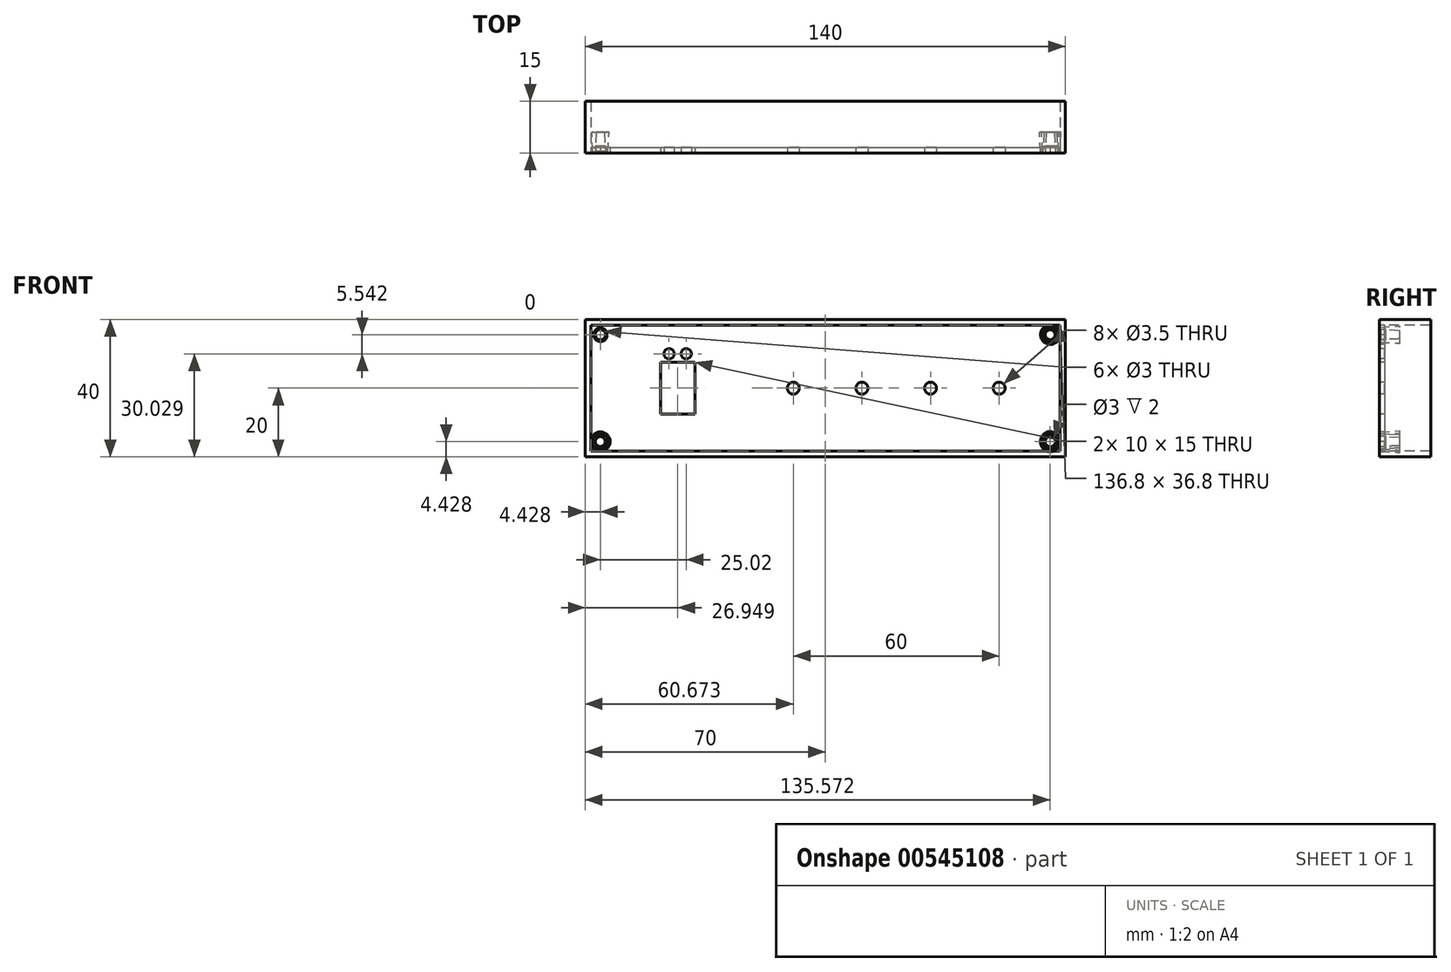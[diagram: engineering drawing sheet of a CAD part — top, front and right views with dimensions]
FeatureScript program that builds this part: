
annotation { "Feature Type Name" : "Feature", "Feature Type Description" : "" }
export const myFeature = defineFeature(function(context is Context, id is Id, definition is map)
    precondition{}
    {
        {
            var Q0;
            Q0=qCreatedBy(makeId("Front.planeOp"),FACE);
            var sketch = newSketch(context, id + "F0", { "sketchPlane" : qUnion([Q0])});
            skLineSegment(sketch, "E0.bottom", {"start": v(-70, 20) * mm, "end": v(70, 20) * mm});
            skLineSegment(sketch, "E0.top", {"start": v(-70, -20) * mm, "end": v(70, -20) * mm});
            skLineSegment(sketch, "E0.left", {"start": v(-70, 20) * mm, "end": v(-70, -20) * mm});
            skLineSegment(sketch, "E0.right", {"start": v(70, 20) * mm, "end": v(70, -20) * mm});
            skPoint(sketch, "E0.middle", {"position": v(0, 0) * mm});
            skLineSegment(sketch, "E1.bottom", {"start": v(-48.05, 7.5) * mm, "end": v(-38.05, 7.5) * mm});
            skLineSegment(sketch, "E1.top", {"start": v(-48.05, -7.5) * mm, "end": v(-38.05, -7.5) * mm});
            skLineSegment(sketch, "E1.left", {"start": v(-48.05, 7.5) * mm, "end": v(-48.05, -7.5) * mm});
            skLineSegment(sketch, "E1.right", {"start": v(-38.05, 7.5) * mm, "end": v(-38.05, -7.5) * mm});
            skPoint(sketch, "E1.middle", {"position": v(-43.05, 0) * mm});
            skCircle(sketch, "E2", {"center": v(-45.55, 10.03) * mm, "radius": 1.5 * mm});
            skCircle(sketch, "E3", {"center": v(-40.55, 10.03) * mm, "radius": 1.5 * mm});
            skPoint(sketch, "E4", {"position": v(-38.05, 0) * mm});
            skCircle(sketch, "E5", {"center": v(-9.33, 0) * mm, "radius": 1.75 * mm});
            skCircle(sketch, "E6", {"center": v(10.67, 0) * mm, "radius": 1.75 * mm});
            skCircle(sketch, "E7", {"center": v(30.67, 0) * mm, "radius": 1.75 * mm});
            skCircle(sketch, "E8", {"center": v(50.67, 0) * mm, "radius": 1.75 * mm});
            skLineSegment(sketch, "E9.0", {"start": v(-68.4, 18.4) * mm, "end": v(68.4, 18.4) * mm});
            skLineSegment(sketch, "E9.1", {"start": v(-68.4, 18.4) * mm, "end": v(-68.4, -18.4) * mm});
            skLineSegment(sketch, "E9.2", {"start": v(-68.4, -18.4) * mm, "end": v(68.4, -18.4) * mm});
            skLineSegment(sketch, "E9.3", {"start": v(68.4, 18.4) * mm, "end": v(68.4, -18.4) * mm});
            skCircle(sketch, "E10.MirrorC", {"center": v(65.57, 15.57) * mm, "radius": 2.83 * mm});
            skCircle(sketch, "E11.MirrorC", {"center": v(65.57, 15.57) * mm, "radius": 1.5 * mm});
            skCircle(sketch, "E12.MirrorC", {"center": v(-65.57, -15.57) * mm, "radius": 1.5 * mm});
            skCircle(sketch, "E13.MirrorC", {"center": v(-65.57, -15.57) * mm, "radius": 2.83 * mm});
            skCircle(sketch, "E14.MirrorC", {"center": v(65.57, -15.57) * mm, "radius": 1.5 * mm});
            skCircle(sketch, "E15.MirrorC", {"center": v(65.57, -15.57) * mm, "radius": 2.83 * mm});
            skCircle(sketch, "E16.MirrorC", {"center": v(65.57, 15.57) * mm, "radius": 2.18 * mm});
            skCircle(sketch, "E17.MirrorC", {"center": v(-65.57, -15.57) * mm, "radius": 2.18 * mm});
            skCircle(sketch, "E18.MirrorC", {"center": v(65.57, -15.57) * mm, "radius": 2.18 * mm});
            skPoint(sketch, "E19", {"position": v(-65.57, 15.57) * mm});
            skSolve(sketch);
        }
        {
            var Q0;
            Q0=makeQuery(id+"F0.imprint","IMPRINT",FACE,{"disambiguationData":[TD([[makeQuery(id+"F0.imprint","IMPRINT",EDGE,{"derivedFrom":sQuery(id+"F0.wireOp",EDGE,"E1.bottom")}),1.0]])]});
            var Q1;
            {var subQ0=sQuery(id+"F0.wireOp",EDGE,"nopY4PQG-6DAR-m26V-C0Me-koIEQxgehs8v");var subQ3=sQuery(id+"F0.wireOp",EDGE,"W0Mv9RJY-RmOc-FBdf-RBb3-klKlk9MDp93k");var subQ5=makeQuery(id+"F0.imprint","INTERSECT",VERTEX,{"derivedFrom":[subQ0,subQ3]});Q1=makeQuery(id+"F0.imprint","IMPRINT",FACE,{"disambiguationData":[TD([[makeQuery(id+"F0.imprint","IMPRINT",EDGE,{"disambiguationData":[TD([[subQ5,1.0]])],"derivedFrom":subQ3}),-1.0]])]});}
            var Q2;
            {var subQ0=sQuery(id+"F0.wireOp",EDGE,"nopY4PQG-6DAR-m26V-C0Me-koIEQxgehs8v");var subQ3=sQuery(id+"F0.wireOp",EDGE,"W0Mv9RJY-RmOc-FBdf-RBb3-klKlk9MDp93k");var subQ5=makeQuery(id+"F0.imprint","INTERSECT",VERTEX,{"derivedFrom":[subQ0,subQ3]});Q2=makeQuery(id+"F0.imprint","IMPRINT",FACE,{"disambiguationData":[TD([[makeQuery(id+"F0.imprint","IMPRINT",EDGE,{"disambiguationData":[TD([[subQ5,-1.0]])],"derivedFrom":subQ3}),-1.0]])]});}
            var Q3;
            {var subQ0=sQuery(id+"F0.wireOp",EDGE,"ZPrOADm0-ys7W-Uhxx-ERF7-CDe04Jh97fXN");var subQ3=sQuery(id+"F0.wireOp",EDGE,"JCLg79E9-NYku-jiiS-Y2hP-Kjt8igKviUym");var subQ5=makeQuery(id+"F0.imprint","INTERSECT",VERTEX,{"derivedFrom":[subQ0,subQ3]});Q3=makeQuery(id+"F0.imprint","IMPRINT",FACE,{"disambiguationData":[TD([[makeQuery(id+"F0.imprint","IMPRINT",EDGE,{"disambiguationData":[TD([[subQ5,1.0]])],"derivedFrom":subQ3}),-1.0]])]});}
            var Q4;
            {var subQ0=sQuery(id+"F0.wireOp",EDGE,"ZPrOADm0-ys7W-Uhxx-ERF7-CDe04Jh97fXN");var subQ3=sQuery(id+"F0.wireOp",EDGE,"JCLg79E9-NYku-jiiS-Y2hP-Kjt8igKviUym");var subQ5=makeQuery(id+"F0.imprint","INTERSECT",VERTEX,{"derivedFrom":[subQ0,subQ3]});Q4=makeQuery(id+"F0.imprint","IMPRINT",FACE,{"disambiguationData":[TD([[makeQuery(id+"F0.imprint","IMPRINT",EDGE,{"disambiguationData":[TD([[subQ5,-1.0]])],"derivedFrom":subQ3}),-1.0]])]});}
            var Q5;
            {var subQ0=sQuery(id+"F0.wireOp",EDGE,"IZJqcF3K-3XQc-JsiF-ESKG-TtM9fcgNwguu");var subQ3=sQuery(id+"F0.wireOp",EDGE,"lmyyJW9V-CXFS-4CVU-ZTqX-mRt5hHccTXIb");var subQ5=makeQuery(id+"F0.imprint","INTERSECT",VERTEX,{"derivedFrom":[subQ0,subQ3]});Q5=makeQuery(id+"F0.imprint","IMPRINT",FACE,{"disambiguationData":[TD([[makeQuery(id+"F0.imprint","IMPRINT",EDGE,{"disambiguationData":[TD([[subQ5,1.0]])],"derivedFrom":subQ3}),-1.0]])]});}
            var Q6;
            {var subQ0=sQuery(id+"F0.wireOp",EDGE,"IZJqcF3K-3XQc-JsiF-ESKG-TtM9fcgNwguu");var subQ3=sQuery(id+"F0.wireOp",EDGE,"lmyyJW9V-CXFS-4CVU-ZTqX-mRt5hHccTXIb");var subQ5=makeQuery(id+"F0.imprint","INTERSECT",VERTEX,{"derivedFrom":[subQ0,subQ3]});Q6=makeQuery(id+"F0.imprint","IMPRINT",FACE,{"disambiguationData":[TD([[makeQuery(id+"F0.imprint","IMPRINT",EDGE,{"disambiguationData":[TD([[subQ5,-1.0]])],"derivedFrom":subQ3}),-1.0]])]});}
            var Q7;
            {var subQ0=sQuery(id+"F0.wireOp",EDGE,"YOfMEWm0-9Egn-xnX8-rI6g-tOub0sCru1eY");var subQ3=sQuery(id+"F0.wireOp",EDGE,"njUcSJY2-imL9-KRpb-pFf1-RJkt4fxxxRg6");var subQ5=makeQuery(id+"F0.imprint","INTERSECT",VERTEX,{"derivedFrom":[subQ0,subQ3]});Q7=makeQuery(id+"F0.imprint","IMPRINT",FACE,{"disambiguationData":[TD([[makeQuery(id+"F0.imprint","IMPRINT",EDGE,{"disambiguationData":[TD([[subQ5,1.0]])],"derivedFrom":subQ3}),-1.0]])]});}
            var Q8;
            {var subQ0=sQuery(id+"F0.wireOp",EDGE,"YOfMEWm0-9Egn-xnX8-rI6g-tOub0sCru1eY");var subQ3=sQuery(id+"F0.wireOp",EDGE,"njUcSJY2-imL9-KRpb-pFf1-RJkt4fxxxRg6");var subQ5=makeQuery(id+"F0.imprint","INTERSECT",VERTEX,{"derivedFrom":[subQ0,subQ3]});Q8=makeQuery(id+"F0.imprint","IMPRINT",FACE,{"disambiguationData":[TD([[makeQuery(id+"F0.imprint","IMPRINT",EDGE,{"disambiguationData":[TD([[subQ5,-1.0]])],"derivedFrom":subQ3}),-1.0]])]});}
            extrude(context, id + "F1", {"entities" : qUnion([Q0, Q1, Q2, Q3, Q4, Q5, Q6, Q7, Q8]), "oppositeDirection" : true, "depth" : 1.6 * mm, "offsetDistance" : 25 * mm});
        }
        {
            var Q0;
            Q0=makeQuery(id+"F0.imprint","IMPRINT",FACE,{"disambiguationData":[TD([[makeQuery(id+"F0.imprint","IMPRINT",EDGE,{"derivedFrom":sQuery(id+"F0.wireOp",EDGE,"E0.bottom")}),-1.0]])]});
            extrude(context, id + "F2", {"entities" : qUnion([Q0]), "oppositeDirection" : true, "depth" : 15 * mm, "offsetDistance" : 25 * mm});
        }
        {
            var Q0;
            Q0=makeQuery(id+"F0.imprint","IMPRINT",FACE,{"disambiguationData":[TD([[makeQuery(id+"F0.imprint","IMPRINT",EDGE,{"derivedFrom":sQuery(id+"F0.wireOp",EDGE,"E1.bottom")}),1.0]])]});
            var Q1;
            {var subQ0=sQuery(id+"F0.wireOp",EDGE,"E9.1");var subQ1=sQuery(id+"F0.wireOp",EDGE,"E9.0");var subQ2=makeQuery(id+"F0.imprint","INTERSECT",VERTEX,{"derivedFrom":[subQ1,subQ0]});Q1=makeQuery(id+"F0.imprint","IMPRINT",FACE,{"disambiguationData":[TD([[makeQuery(id+"F0.imprint","IMPRINT",EDGE,{"disambiguationData":[TD([[subQ2,-1.0]])],"derivedFrom":subQ1}),-1.0]])]});}
            var Q2;
            {var subQ0=sQuery(id+"F0.wireOp",EDGE,"E9.2");var subQ1=sQuery(id+"F0.wireOp",EDGE,"E9.1");var subQ2=makeQuery(id+"F0.imprint","INTERSECT",VERTEX,{"derivedFrom":[subQ1,subQ0]});Q2=makeQuery(id+"F0.imprint","IMPRINT",FACE,{"disambiguationData":[TD([[makeQuery(id+"F0.imprint","IMPRINT",EDGE,{"disambiguationData":[TD([[subQ2,1.0]])],"derivedFrom":subQ1}),1.0]])]});}
            var Q3;
            {var subQ0=sQuery(id+"F0.wireOp",EDGE,"E9.3");var subQ1=sQuery(id+"F0.wireOp",EDGE,"E9.2");var subQ2=makeQuery(id+"F0.imprint","INTERSECT",VERTEX,{"derivedFrom":[subQ1,subQ0]});Q3=makeQuery(id+"F0.imprint","IMPRINT",FACE,{"disambiguationData":[TD([[makeQuery(id+"F0.imprint","IMPRINT",EDGE,{"disambiguationData":[TD([[subQ2,1.0]])],"derivedFrom":subQ1}),1.0]])]});}
            var Q4;
            {var subQ0=sQuery(id+"F0.wireOp",EDGE,"E9.3");var subQ1=sQuery(id+"F0.wireOp",EDGE,"E9.0");var subQ2=makeQuery(id+"F0.imprint","INTERSECT",VERTEX,{"derivedFrom":[subQ1,subQ0]});Q4=makeQuery(id+"F0.imprint","IMPRINT",FACE,{"disambiguationData":[TD([[makeQuery(id+"F0.imprint","IMPRINT",EDGE,{"disambiguationData":[TD([[subQ2,1.0]])],"derivedFrom":subQ1}),-1.0]])]});}
            extrude(context, id + "F3", {"entities" : qUnion([Q0, Q1, Q2, Q3, Q4]), "oppositeDirection" : true, "depth" : 1.6 * mm, "offsetDistance" : 25 * mm});
        }
        {
            var Q0;
            Q0=makeQuery(id+"F0.imprint","IMPRINT",FACE,{"disambiguationData":[TD([[makeQuery(id+"F0.imprint","IMPRINT",EDGE,{"derivedFrom":sQuery(id+"F0.wireOp",EDGE,"E16.MirrorC")}),1.0]])]});
            var Q1;
            Q1=makeQuery(id+"F0.imprint","IMPRINT",FACE,{"disambiguationData":[TD([[makeQuery(id+"F0.imprint","IMPRINT",EDGE,{"derivedFrom":sQuery(id+"F0.wireOp",EDGE,"E18.MirrorC")}),-1.0]])]});
            var Q2;
            Q2=makeQuery(id+"F0.imprint","IMPRINT",FACE,{"disambiguationData":[TD([[makeQuery(id+"F0.imprint","IMPRINT",EDGE,{"derivedFrom":sQuery(id+"F0.wireOp",EDGE,"E17.MirrorC")}),1.0]])]});
            var Q3;
            Q3=makeQuery(id+"F0.imprint","IMPRINT",FACE,{"disambiguationData":[TD([[makeQuery(id+"F0.imprint","IMPRINT",EDGE,{"derivedFrom":sQuery(id+"F0.wireOp",EDGE,"Fbiw61Zs-MAMp-hI35-5nYk-Zl3KmD03x1qN")}),-1.0]])]});
            extrude(context, id + "F4", {"entities" : qUnion([Q0, Q1, Q2, Q3]), "oppositeDirection" : true, "depth" : 6 * mm, "offsetDistance" : 25 * mm, "hasDraft" : true, "draftAngle" : 3 * degree});
        }
        {
            var Q0;
            Q0=makeQuery(id+"F0.imprint","IMPRINT",FACE,{"disambiguationData":[TD([[makeQuery(id+"F0.imprint","IMPRINT",EDGE,{"derivedFrom":sQuery(id+"F0.wireOp",EDGE,"E11.MirrorC")}),1.0]])]});
            var Q1;
            Q1=makeQuery(id+"F0.imprint","IMPRINT",FACE,{"disambiguationData":[TD([[makeQuery(id+"F0.imprint","IMPRINT",EDGE,{"derivedFrom":sQuery(id+"F0.wireOp",EDGE,"E14.MirrorC")}),-1.0]])]});
            var Q2;
            Q2=makeQuery(id+"F0.imprint","IMPRINT",FACE,{"disambiguationData":[TD([[makeQuery(id+"F0.imprint","IMPRINT",EDGE,{"derivedFrom":sQuery(id+"F0.wireOp",EDGE,"E12.MirrorC")}),1.0]])]});
            var Q3;
            Q3=makeQuery(id+"F0.imprint","IMPRINT",FACE,{"disambiguationData":[TD([[makeQuery(id+"F0.imprint","IMPRINT",EDGE,{"derivedFrom":sQuery(id+"F0.wireOp",EDGE,"i0ny2WgH-6vAy-kXJC-6UUB-w2G9uGSbP7yn")}),-1.0]])]});
            extrude(context, id + "F5", {"entities" : qUnion([Q0, Q1, Q2, Q3]), "oppositeDirection" : true, "depth" : 2 * mm, "offsetDistance" : 25 * mm});
        }
        {
            var Q0;
            Q0=sQuery(id+"F0.wireOp",VERTEX,"E19");
            var Q1;
            Q1=makeQuery(id+"F1.opExtrude","SWEPT_BODY",BODY,{"disambiguationData":[OSD([sQuery(id+"F0.wireOp",EDGE,"E1.bottom"),sQuery(id+"F0.wireOp",EDGE,"E1.top"),sQuery(id+"F0.wireOp",EDGE,"E1.left"),sQuery(id+"F0.wireOp",EDGE,"E1.right"),sQuery(id+"F0.wireOp",EDGE,"E2"),sQuery(id+"F0.wireOp",EDGE,"E3"),sQuery(id+"F0.wireOp",EDGE,"E5"),sQuery(id+"F0.wireOp",EDGE,"E6"),sQuery(id+"F0.wireOp",EDGE,"E7"),sQuery(id+"F0.wireOp",EDGE,"E8"),sQuery(id+"F0.wireOp",EDGE,"E9.0"),sQuery(id+"F0.wireOp",EDGE,"E9.1"),sQuery(id+"F0.wireOp",EDGE,"E9.2"),sQuery(id+"F0.wireOp",EDGE,"E9.3"),sQuery(id+"F0.wireOp",EDGE,"E10.MirrorC"),sQuery(id+"F0.wireOp",EDGE,"E13.MirrorC"),sQuery(id+"F0.wireOp",EDGE,"E15.MirrorC")])]});
            var Q2;
            Q2=makeQuery(id+"F3.opExtrude","SWEPT_BODY",BODY,{"disambiguationData":[OSD([sQuery(id+"F0.wireOp",EDGE,"E1.bottom"),sQuery(id+"F0.wireOp",EDGE,"E1.top"),sQuery(id+"F0.wireOp",EDGE,"E1.left"),sQuery(id+"F0.wireOp",EDGE,"E1.right"),sQuery(id+"F0.wireOp",EDGE,"E2"),sQuery(id+"F0.wireOp",EDGE,"E3"),sQuery(id+"F0.wireOp",EDGE,"E5"),sQuery(id+"F0.wireOp",EDGE,"E6"),sQuery(id+"F0.wireOp",EDGE,"E7"),sQuery(id+"F0.wireOp",EDGE,"E8"),sQuery(id+"F0.wireOp",EDGE,"E9.0"),sQuery(id+"F0.wireOp",EDGE,"E9.1"),sQuery(id+"F0.wireOp",EDGE,"E9.2"),sQuery(id+"F0.wireOp",EDGE,"E9.3"),sQuery(id+"F0.wireOp",EDGE,"E10.MirrorC"),sQuery(id+"F0.wireOp",EDGE,"E13.MirrorC"),sQuery(id+"F0.wireOp",EDGE,"E15.MirrorC")])]});
            hole(context, id + "F6", {"style" : HoleStyle.C_SINK, "endStyle" : HoleEndStyle.THROUGH, "holeDiameter" : 3 * mm, "cSinkDiameter" : 4 * mm, "cSinkAngle" : 90 * degree, "isTappedThrough" : true, "tappedDepth" : 12 * mm, "tapClearance" : 3, "locations" : qUnion([Q0]), "scope" : qUnion([Q1, Q2])});
        }
    });
